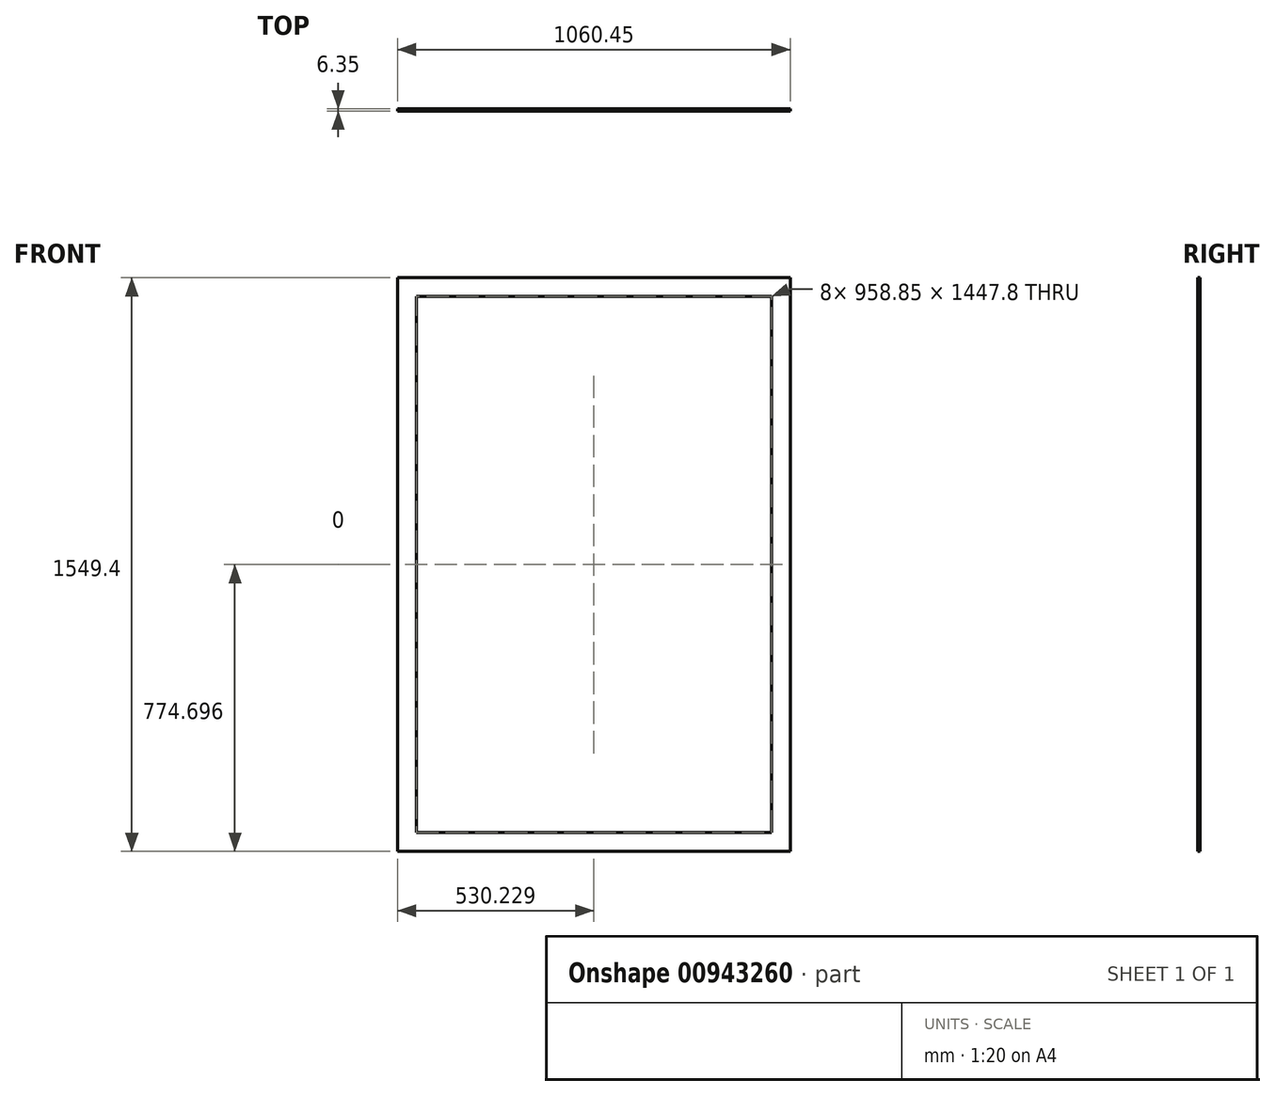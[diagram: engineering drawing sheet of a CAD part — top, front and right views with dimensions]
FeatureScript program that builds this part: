
annotation { "Feature Type Name" : "Feature", "Feature Type Description" : "" }
export const myFeature = defineFeature(function(context is Context, id is Id, definition is map)
    precondition{}
    {
        {
            var Q0;
            Q0=qCreatedBy(makeId("Front.planeOp"),FACE);
            var sketch = newSketch(context, id + "F0", { "sketchPlane" : qUnion([Q0])});
            skLineSegment(sketch, "E0.bottom", {"start": v(-528.57, 984.12) * mm, "end": v(531.88, 984.12) * mm});
            skLineSegment(sketch, "E0.top", {"start": v(-528.57, -565.28) * mm, "end": v(531.88, -565.28) * mm});
            skLineSegment(sketch, "E0.left", {"start": v(-528.57, 984.12) * mm, "end": v(-528.57, -565.28) * mm});
            skLineSegment(sketch, "E0.right", {"start": v(531.88, 984.12) * mm, "end": v(531.88, -565.28) * mm});
            skLineSegment(sketch, "E1.0", {"start": v(-477.77, 933.32) * mm, "end": v(481.08, 933.32) * mm});
            skLineSegment(sketch, "E1.1", {"start": v(-477.77, 933.32) * mm, "end": v(-477.77, -514.48) * mm});
            skLineSegment(sketch, "E1.2", {"start": v(-477.77, -514.48) * mm, "end": v(481.08, -514.48) * mm});
            skLineSegment(sketch, "E1.3", {"start": v(481.08, 933.32) * mm, "end": v(481.08, -514.48) * mm});
            skSolve(sketch);
        }
        {
            var Q0;
            Q0=makeQuery(id+"F0.imprint","IMPRINT",FACE,{"disambiguationData":[TD([[makeQuery(id+"F0.imprint","IMPRINT",EDGE,{"derivedFrom":sQuery(id+"F0.wireOp",EDGE,"E0.bottom")}),-1.0]])]});
            extrude(context, id + "F1", {"entities" : qUnion([Q0]), "depth" : 6.35 * mm, "offsetDistance" : 25.4 * mm});
        }
    });
